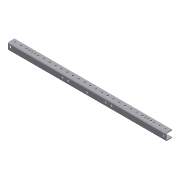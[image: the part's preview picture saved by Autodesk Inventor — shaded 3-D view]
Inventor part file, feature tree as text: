
AUTODESK INVENTOR PART (.ipt)
format: ipt  version: 2013 (Build 170138000, 138)  size: 395,264 bytes
history: native  units: in
note: dims shown in document units (in); Inventor stores cm internally (conversion verified against a paired STEP export)
features: sheet_metal_op x8, sketch x7, other x4, projected_geometry x4, hole x3, pattern_linear x1, mirror x1
ambient origin geometry x8: Origin, YZ Plane, XZ Plane, XY Plane, X Axis, Y Axis, Z Axis, Center Point
feature tree (28):
  sheet_metal_op  "Face2"
  sheet_metal_op  "Flange1"
  sheet_metal_op  "Unfold1"
  hole  "Hole1"  [1 undecoded]
  pattern_linear  "Rectangular Pattern1"  Spacing1=1.125in  [1 undecoded]
  hole  "Hole2"  [1 undecoded]
  sheet_metal_op  "Refold1"
  sheet_metal_op  "Unfold2"
  sheet_metal_op  "Refold2"
  hole  "Hole3"  [1 undecoded]
  mirror  "Mirror1"
  sketch  "Sketch3"  dims[d4=0.75in]
  other  "Plate2"
  sketch  "Sketch4"  dims[d5=0.125in]
  other  "Plate3"
  sheet_metal_op  "Bend1"
  sheet_metal_op  "Corner1"
  sketch  "Sketch6"  dims[d6=0.125in]
  projected_geometry  "Projected Loop1"
  projected_geometry  "Projected Loop2"
  projected_geometry  "Projected Loop3"
  projected_geometry  "Projected Loop4"
  sketch  "Sketch7"  dims[d7=0.0625in]
  sketch  "Sketch8"  dims[d8=0.25in]
  sketch  "Sketch9"  dims[d9=0.125in d10=1.125in d11=90.0deg d12=0.125in d13=0.5in d14=0.125in d15=0.125in d19=0.5in d20=0.5in d21=0.5in d22=0.5in d23=0.257in d24=0.75in d25=0.375in d26=0.25in d27=0.5635in d28=0.125in d29=0.8108in d30=13.7795in d32=1.0in d33=3.25in d34=4.25in d35=13.25in d36=14.25in d37=1.458in d38=1.608in d39=0.38in d40=0.75in d41=0.375in d42=0.25in d43=0.5635in d44=0.125in d45=0.8108in d46=3.875in d47=3.875in d48=0.125in d49=0.0in d50=0.5in d51=1.0in d52=0.25in d53=0.75in d54=0.375in d55=0.25in d56=0.5635in d57=0.125in d58=0.8108in]
  other  "Cut1"
  other  "Definition1"
  sketch  "Sketch1"  dims[d2=0.125in d3=35.0in]
note: 4 required parameter values undecoded (feature->parameter linkage not recoverable at this tier; creation-order binding heuristic only, values carry confidence <= 0.55)
